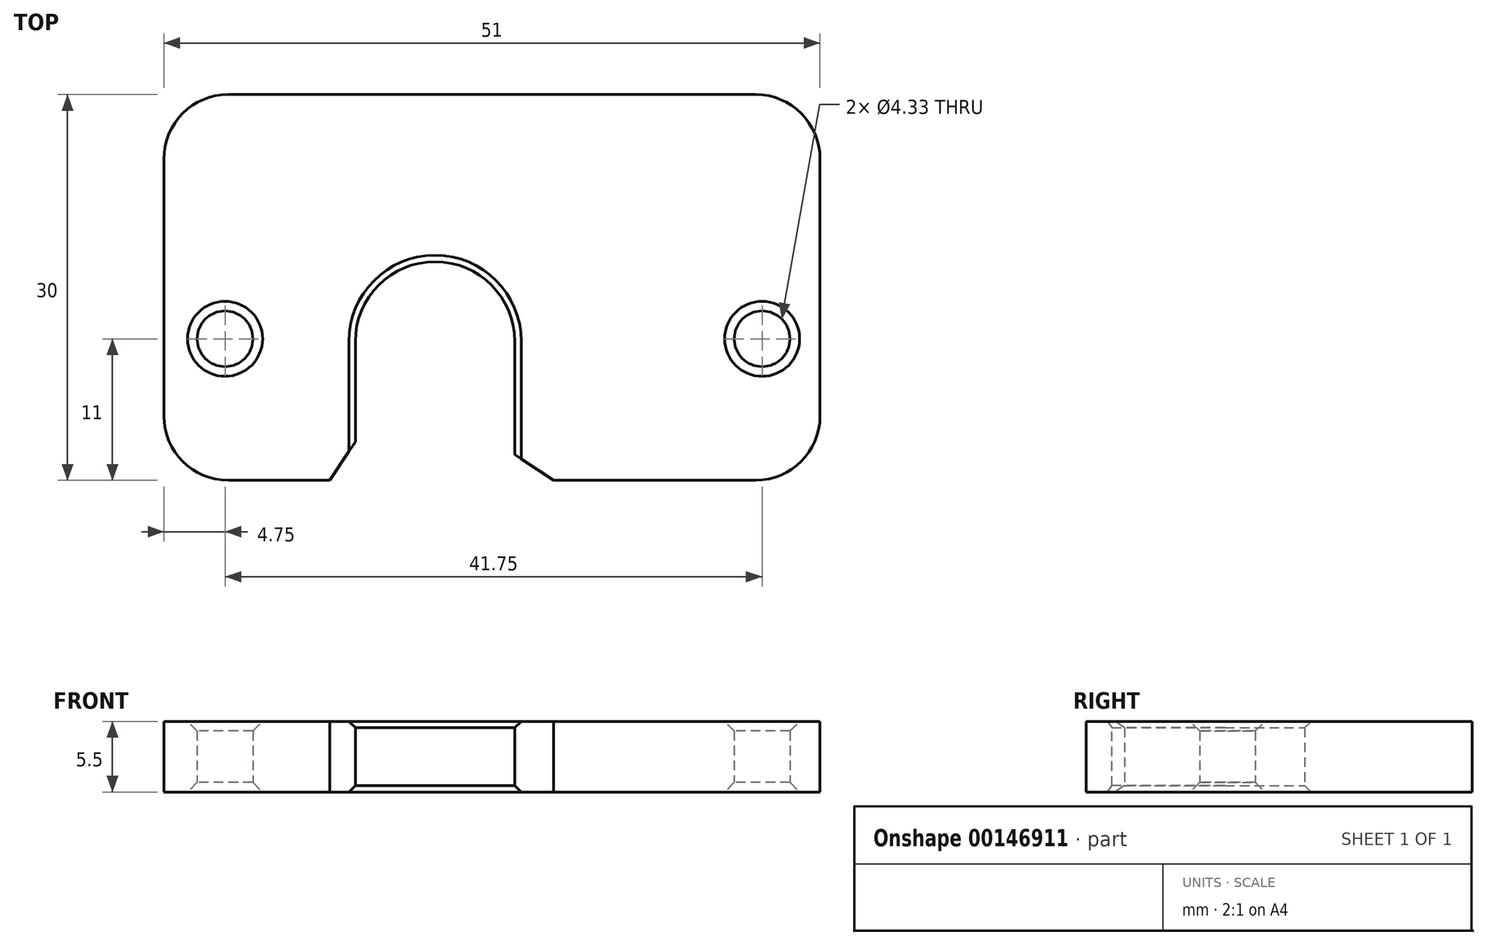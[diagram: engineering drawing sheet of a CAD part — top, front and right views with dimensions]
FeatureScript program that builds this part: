
annotation { "Feature Type Name" : "Feature", "Feature Type Description" : "" }
export const myFeature = defineFeature(function(context is Context, id is Id, definition is map)
    precondition{}
    {
        {
            var Q0;
            Q0=qCreatedBy(makeId("Top.planeOp"),FACE);
            var sketch = newSketch(context, id + "F0", { "sketchPlane" : qUnion([Q0])});
            skLineSegment(sketch, "E0.bottom", {"start": v(-25.5, 11) * mm, "end": v(25.5, 11) * mm});
            skLineSegment(sketch, "E0.top", {"start": v(-25.5, -11) * mm, "end": v(-10.62, -11) * mm});
            skLineSegment(sketch, "E0.left", {"start": v(-25.5, 11) * mm, "end": v(-25.5, -11) * mm});
            skLineSegment(sketch, "E0.right", {"start": v(25.5, 11) * mm, "end": v(25.5, -11) * mm});
            skArc(sketch, "E1", {"start": v(1.77, -0.2) * mm, "mid": v(-4.43, 6) * mm, "end": v(-10.63, -0.2) * mm});
            skLineSegment(sketch, "E2", {"start": v(-10.63, -0.2) * mm, "end": v(-10.62, -11) * mm});
            skLineSegment(sketch, "E3", {"start": v(1.77, -0.2) * mm, "end": v(1.78, -11) * mm});
            skLineSegment(sketch, "E4.trimOffspring", {"start": v(1.78, -11) * mm, "end": v(25.5, -11) * mm});
            skCircle(sketch, "E5", {"center": v(-20.75, 0) * mm, "radius": 2.17 * mm});
            skPoint(sketch, "E6.centerSnap0", {"position": v(-25.5, 0) * mm});
            skCircle(sketch, "E7", {"center": v(21, 0) * mm, "radius": 2.17 * mm});
            skSolve(sketch);
        }
        {
            var Q0;
            Q0=qSketchRegion(id+"F0",true);
            extrude(context, id + "F1", {"entities" : qUnion([Q0]), "depth" : 5.5 * mm});
        }
        {
            var Q0;
            Q0=makeQuery(id+"F1.opExtrude","CAP_EDGE",EDGE,{"disambiguationData":[OSD([sQuery(id+"F0.wireOp",EDGE,"E5")])],"isStart":true});
            var Q1;
            Q1=makeQuery(id+"F1.opExtrude","CAP_EDGE",EDGE,{"disambiguationData":[OSD([sQuery(id+"F0.wireOp",EDGE,"E7")])],"isStart":true});
            var Q2;
            Q2=makeQuery(id+"F1.opExtrude","CAP_EDGE",EDGE,{"disambiguationData":[OSD([sQuery(id+"F0.wireOp",EDGE,"E7")])],"isStart":false});
            var Q3;
            Q3=makeQuery(id+"F1.opExtrude","CAP_EDGE",EDGE,{"disambiguationData":[OSD([sQuery(id+"F0.wireOp",EDGE,"E5")])],"isStart":false});
            chamfer(context, id + "F2", {"entities" : qUnion([Q0, Q1, Q2, Q3]), "width" : .75 * mm, "tangentPropagation" : true});
        }
        {
            var Q0;
            Q0=qCreatedBy(makeId("Top.planeOp"),FACE);
            var sketch = newSketch(context, id + "F3", { "sketchPlane" : qUnion([Q0])});
            skLineSegment(sketch, "E8.0", {"start": v(-25.5, 11) * mm, "end": v(25.5, 11) * mm});
            skLineSegment(sketch, "E9", {"start": v(-25.5, 11) * mm, "end": v(-25.5, 19) * mm});
            skLineSegment(sketch, "E10", {"start": v(-25.5, 19) * mm, "end": v(25.5, 19) * mm});
            skLineSegment(sketch, "E11", {"start": v(25.5, 19) * mm, "end": v(25.5, 11) * mm});
            skSolve(sketch);
        }
        {
            var Q0;
            Q0=qSketchRegion(id+"F3",true);
            var Q1;
            Q1=makeQuery(id+"F1.opExtrude","CAP_FACE",FACE,{"disambiguationData":[OSD([sQuery(id+"F0.wireOp",EDGE,"E0.bottom"),sQuery(id+"F0.wireOp",EDGE,"E0.top"),sQuery(id+"F0.wireOp",EDGE,"E0.left"),sQuery(id+"F0.wireOp",EDGE,"E0.right"),sQuery(id+"F0.wireOp",EDGE,"E1"),sQuery(id+"F0.wireOp",EDGE,"E2"),sQuery(id+"F0.wireOp",EDGE,"E3"),sQuery(id+"F0.wireOp",EDGE,"E4.trimOffspring"),sQuery(id+"F0.wireOp",EDGE,"E5"),sQuery(id+"F0.wireOp",EDGE,"E7")])],"isStart":false});
            extrude(context, id + "F4", {"entities" : qUnion([Q0]), "operationType" : NewBodyOperationType.ADD, "endBound" : BoundingType.UP_TO_SURFACE, "endBoundEntityFace" : qUnion([Q1]), "depth" : 6 * mm});
        }
        {
            var Q0;
            Q0=makeQuery(id+"F1.opExtrude","CAP_EDGE",EDGE,{"disambiguationData":[OSD([sQuery(id+"F0.wireOp",EDGE,"E1")])],"isStart":false});
            var Q1;
            Q1=makeQuery(id+"F1.opExtrude","CAP_EDGE",EDGE,{"disambiguationData":[OSD([sQuery(id+"F0.wireOp",EDGE,"E1")])],"isStart":true});
            var Q2;
            Q2=makeQuery(id+"F1.opExtrude","CAP_EDGE",EDGE,{"disambiguationData":[OSD([sQuery(id+"F0.wireOp",EDGE,"E2")])],"isStart":false});
            var Q3;
            {var subQ0=sQuery(id+"F0.wireOp",EDGE,"E7");var subQ1=sQuery(id+"F0.wireOp",EDGE,"E5");var subQ2=sQuery(id+"F0.wireOp",EDGE,"E4.trimOffspring");var subQ3=sQuery(id+"F0.wireOp",EDGE,"E3");var subQ4=sQuery(id+"F0.wireOp",EDGE,"E2");var subQ5=sQuery(id+"F0.wireOp",EDGE,"E1");var subQ6=sQuery(id+"F0.wireOp",EDGE,"E0.right");var subQ7=sQuery(id+"F0.wireOp",EDGE,"E0.left");var subQ8=sQuery(id+"F0.wireOp",EDGE,"E0.top");var subQ9=sQuery(id+"F0.wireOp",EDGE,"E0.bottom");Q3=makeQuery(id+"F8.opChamfer","BLEND_EDGE",EDGE,{"blendedFrom":[makeQuery(id+"F1.opExtrude","SWEPT_EDGE",EDGE,{"disambiguationData":[OSD([subQ8,subQ4])]}),makeQuery(id+"F4.boolean.opBoolean","MERGE",FACE,{"derivedFrom":[makeQuery(id+"F1.opExtrude","CAP_FACE",FACE,{"disambiguationData":[OSD([subQ9,subQ8,subQ7,subQ6,subQ5,subQ4,subQ3,subQ2,subQ1,subQ0])],"isStart":false}),makeQuery(id+"F4.opExtrude","CAP_FACE",FACE,{"disambiguationData":[OSD([subQ9,subQ8,subQ7,subQ6,subQ5,subQ4,subQ3,subQ2,subQ1,subQ0])],"isStart":false})]})],"blendedInto":[makeQuery(id+"F4.boolean.opBoolean","MERGE",FACE,{"derivedFrom":[makeQuery(id+"F1.opExtrude","CAP_FACE",FACE,{"disambiguationData":[OSD([subQ9,subQ8,subQ7,subQ6,subQ5,subQ4,subQ3,subQ2,subQ1,subQ0])],"isStart":false}),makeQuery(id+"F4.opExtrude","CAP_FACE",FACE,{"disambiguationData":[OSD([subQ9,subQ8,subQ7,subQ6,subQ5,subQ4,subQ3,subQ2,subQ1,subQ0])],"isStart":false})]})]});}
            var Q4;
            {var subQ0=sQuery(id+"F0.wireOp",EDGE,"E2");var subQ1=sQuery(id+"F0.wireOp",EDGE,"E0.top");Q4=makeQuery(id+"F8.opChamfer","BLEND_EDGE",EDGE,{"blendedFrom":[makeQuery(id+"F1.opExtrude","SWEPT_EDGE",EDGE,{"disambiguationData":[OSD([subQ1,subQ0])]}),makeQuery(id+"FEx9i5uBCyc1I2h_1.boolean.opBoolean","MERGE",FACE,{"derivedFrom":[makeQuery(id+"F4.boolean.opBoolean","MERGE",FACE,{"derivedFrom":[makeQuery(id+"F1.opExtrude","CAP_FACE",FACE,{"disambiguationData":[OSD([sQuery(id+"F0.wireOp",EDGE,"E0.bottom"),subQ1,sQuery(id+"F0.wireOp",EDGE,"E0.left"),sQuery(id+"F0.wireOp",EDGE,"E0.right"),sQuery(id+"F0.wireOp",EDGE,"E1"),subQ0,sQuery(id+"F0.wireOp",EDGE,"E3"),sQuery(id+"F0.wireOp",EDGE,"E4.trimOffspring"),sQuery(id+"F0.wireOp",EDGE,"E5"),sQuery(id+"F0.wireOp",EDGE,"E7")])],"isStart":true}),makeQuery(id+"F4.opExtrude","CAP_FACE",FACE,{"disambiguationData":[OSD([sQuery(id+"F3.wireOp",EDGE,"E8.0"),sQuery(id+"F3.wireOp",EDGE,"E9"),sQuery(id+"F3.wireOp",EDGE,"E10"),sQuery(id+"F3.wireOp",EDGE,"E11")])],"isStart":true})]}),makeQuery(id+"FEx9i5uBCyc1I2h_1.opExtrude","CAP_FACE",FACE,{"disambiguationData":[OSD([sQuery(id+"F6.wireOp",EDGE,"E15"),sQuery(id+"F6.wireOp",EDGE,"E16"),sQuery(id+"F6.wireOp",EDGE,"E17"),sQuery(id+"F6.wireOp",EDGE,"E18")])],"isStart":true}),makeQuery(id+"FEx9i5uBCyc1I2h_1.opExtrude","CAP_FACE",FACE,{"disambiguationData":[OSD([sQuery(id+"F6.wireOp",EDGE,"E19.MirrorCS"),sQuery(id+"F6.wireOp",EDGE,"E20.MirrorCS"),sQuery(id+"F6.wireOp",EDGE,"E21.MirrorCS"),sQuery(id+"F6.wireOp",EDGE,"E23.MirrorCS")])],"isStart":true})]})],"blendedInto":[makeQuery(id+"FEx9i5uBCyc1I2h_1.boolean.opBoolean","MERGE",FACE,{"derivedFrom":[makeQuery(id+"F4.boolean.opBoolean","MERGE",FACE,{"derivedFrom":[makeQuery(id+"F1.opExtrude","CAP_FACE",FACE,{"disambiguationData":[OSD([sQuery(id+"F0.wireOp",EDGE,"E0.bottom"),subQ1,sQuery(id+"F0.wireOp",EDGE,"E0.left"),sQuery(id+"F0.wireOp",EDGE,"E0.right"),sQuery(id+"F0.wireOp",EDGE,"E1"),subQ0,sQuery(id+"F0.wireOp",EDGE,"E3"),sQuery(id+"F0.wireOp",EDGE,"E4.trimOffspring"),sQuery(id+"F0.wireOp",EDGE,"E5"),sQuery(id+"F0.wireOp",EDGE,"E7")])],"isStart":true}),makeQuery(id+"F4.opExtrude","CAP_FACE",FACE,{"disambiguationData":[OSD([sQuery(id+"F3.wireOp",EDGE,"E8.0"),sQuery(id+"F3.wireOp",EDGE,"E9"),sQuery(id+"F3.wireOp",EDGE,"E10"),sQuery(id+"F3.wireOp",EDGE,"E11")])],"isStart":true})]}),makeQuery(id+"FEx9i5uBCyc1I2h_1.opExtrude","CAP_FACE",FACE,{"disambiguationData":[OSD([sQuery(id+"F6.wireOp",EDGE,"E15"),sQuery(id+"F6.wireOp",EDGE,"E16"),sQuery(id+"F6.wireOp",EDGE,"E17"),sQuery(id+"F6.wireOp",EDGE,"E18")])],"isStart":true}),makeQuery(id+"FEx9i5uBCyc1I2h_1.opExtrude","CAP_FACE",FACE,{"disambiguationData":[OSD([sQuery(id+"F6.wireOp",EDGE,"E19.MirrorCS"),sQuery(id+"F6.wireOp",EDGE,"E20.MirrorCS"),sQuery(id+"F6.wireOp",EDGE,"E21.MirrorCS"),sQuery(id+"F6.wireOp",EDGE,"E23.MirrorCS")])],"isStart":true})]})]});}
            var Q5;
            Q5=makeQuery(id+"F1.opExtrude","CAP_EDGE",EDGE,{"disambiguationData":[OSD([sQuery(id+"F0.wireOp",EDGE,"E2")])],"isStart":true});
            var Q6;
            Q6=makeQuery(id+"F1.opExtrude","CAP_EDGE",EDGE,{"disambiguationData":[OSD([sQuery(id+"F0.wireOp",EDGE,"E3")])],"isStart":true});
            var Q7;
            {var subQ0=sQuery(id+"F0.wireOp",EDGE,"E4.trimOffspring");var subQ1=sQuery(id+"F0.wireOp",EDGE,"E3");Q7=makeQuery(id+"F8.opChamfer","BLEND_EDGE",EDGE,{"blendedFrom":[makeQuery(id+"F1.opExtrude","SWEPT_EDGE",EDGE,{"disambiguationData":[OSD([subQ1,subQ0])]}),makeQuery(id+"FEx9i5uBCyc1I2h_1.boolean.opBoolean","MERGE",FACE,{"derivedFrom":[makeQuery(id+"F4.boolean.opBoolean","MERGE",FACE,{"derivedFrom":[makeQuery(id+"F1.opExtrude","CAP_FACE",FACE,{"disambiguationData":[OSD([sQuery(id+"F0.wireOp",EDGE,"E0.bottom"),sQuery(id+"F0.wireOp",EDGE,"E0.top"),sQuery(id+"F0.wireOp",EDGE,"E0.left"),sQuery(id+"F0.wireOp",EDGE,"E0.right"),sQuery(id+"F0.wireOp",EDGE,"E1"),sQuery(id+"F0.wireOp",EDGE,"E2"),subQ1,subQ0,sQuery(id+"F0.wireOp",EDGE,"E5"),sQuery(id+"F0.wireOp",EDGE,"E7")])],"isStart":true}),makeQuery(id+"F4.opExtrude","CAP_FACE",FACE,{"disambiguationData":[OSD([sQuery(id+"F3.wireOp",EDGE,"E8.0"),sQuery(id+"F3.wireOp",EDGE,"E9"),sQuery(id+"F3.wireOp",EDGE,"E10"),sQuery(id+"F3.wireOp",EDGE,"E11")])],"isStart":true})]}),makeQuery(id+"FEx9i5uBCyc1I2h_1.opExtrude","CAP_FACE",FACE,{"disambiguationData":[OSD([sQuery(id+"F6.wireOp",EDGE,"E15"),sQuery(id+"F6.wireOp",EDGE,"E16"),sQuery(id+"F6.wireOp",EDGE,"E17"),sQuery(id+"F6.wireOp",EDGE,"E18")])],"isStart":true}),makeQuery(id+"FEx9i5uBCyc1I2h_1.opExtrude","CAP_FACE",FACE,{"disambiguationData":[OSD([sQuery(id+"F6.wireOp",EDGE,"E19.MirrorCS"),sQuery(id+"F6.wireOp",EDGE,"E20.MirrorCS"),sQuery(id+"F6.wireOp",EDGE,"E21.MirrorCS"),sQuery(id+"F6.wireOp",EDGE,"E23.MirrorCS")])],"isStart":true})]})],"blendedInto":[makeQuery(id+"FEx9i5uBCyc1I2h_1.boolean.opBoolean","MERGE",FACE,{"derivedFrom":[makeQuery(id+"F4.boolean.opBoolean","MERGE",FACE,{"derivedFrom":[makeQuery(id+"F1.opExtrude","CAP_FACE",FACE,{"disambiguationData":[OSD([sQuery(id+"F0.wireOp",EDGE,"E0.bottom"),sQuery(id+"F0.wireOp",EDGE,"E0.top"),sQuery(id+"F0.wireOp",EDGE,"E0.left"),sQuery(id+"F0.wireOp",EDGE,"E0.right"),sQuery(id+"F0.wireOp",EDGE,"E1"),sQuery(id+"F0.wireOp",EDGE,"E2"),subQ1,subQ0,sQuery(id+"F0.wireOp",EDGE,"E5"),sQuery(id+"F0.wireOp",EDGE,"E7")])],"isStart":true}),makeQuery(id+"F4.opExtrude","CAP_FACE",FACE,{"disambiguationData":[OSD([sQuery(id+"F3.wireOp",EDGE,"E8.0"),sQuery(id+"F3.wireOp",EDGE,"E9"),sQuery(id+"F3.wireOp",EDGE,"E10"),sQuery(id+"F3.wireOp",EDGE,"E11")])],"isStart":true})]}),makeQuery(id+"FEx9i5uBCyc1I2h_1.opExtrude","CAP_FACE",FACE,{"disambiguationData":[OSD([sQuery(id+"F6.wireOp",EDGE,"E15"),sQuery(id+"F6.wireOp",EDGE,"E16"),sQuery(id+"F6.wireOp",EDGE,"E17"),sQuery(id+"F6.wireOp",EDGE,"E18")])],"isStart":true}),makeQuery(id+"FEx9i5uBCyc1I2h_1.opExtrude","CAP_FACE",FACE,{"disambiguationData":[OSD([sQuery(id+"F6.wireOp",EDGE,"E19.MirrorCS"),sQuery(id+"F6.wireOp",EDGE,"E20.MirrorCS"),sQuery(id+"F6.wireOp",EDGE,"E21.MirrorCS"),sQuery(id+"F6.wireOp",EDGE,"E23.MirrorCS")])],"isStart":true})]})]});}
            var Q8;
            Q8=makeQuery(id+"F1.opExtrude","CAP_EDGE",EDGE,{"disambiguationData":[OSD([sQuery(id+"F0.wireOp",EDGE,"E3")])],"isStart":false});
            var Q9;
            {var subQ0=sQuery(id+"F0.wireOp",EDGE,"E7");var subQ1=sQuery(id+"F0.wireOp",EDGE,"E5");var subQ2=sQuery(id+"F0.wireOp",EDGE,"E4.trimOffspring");var subQ3=sQuery(id+"F0.wireOp",EDGE,"E3");var subQ4=sQuery(id+"F0.wireOp",EDGE,"E2");var subQ5=sQuery(id+"F0.wireOp",EDGE,"E1");var subQ6=sQuery(id+"F0.wireOp",EDGE,"E0.right");var subQ7=sQuery(id+"F0.wireOp",EDGE,"E0.left");var subQ8=sQuery(id+"F0.wireOp",EDGE,"E0.top");var subQ9=sQuery(id+"F0.wireOp",EDGE,"E0.bottom");Q9=makeQuery(id+"F8.opChamfer","BLEND_EDGE",EDGE,{"blendedFrom":[makeQuery(id+"F1.opExtrude","SWEPT_EDGE",EDGE,{"disambiguationData":[OSD([subQ3,subQ2])]}),makeQuery(id+"F4.boolean.opBoolean","MERGE",FACE,{"derivedFrom":[makeQuery(id+"F1.opExtrude","CAP_FACE",FACE,{"disambiguationData":[OSD([subQ9,subQ8,subQ7,subQ6,subQ5,subQ4,subQ3,subQ2,subQ1,subQ0])],"isStart":false}),makeQuery(id+"F4.opExtrude","CAP_FACE",FACE,{"disambiguationData":[OSD([subQ9,subQ8,subQ7,subQ6,subQ5,subQ4,subQ3,subQ2,subQ1,subQ0])],"isStart":false})]})],"blendedInto":[makeQuery(id+"F4.boolean.opBoolean","MERGE",FACE,{"derivedFrom":[makeQuery(id+"F1.opExtrude","CAP_FACE",FACE,{"disambiguationData":[OSD([subQ9,subQ8,subQ7,subQ6,subQ5,subQ4,subQ3,subQ2,subQ1,subQ0])],"isStart":false}),makeQuery(id+"F4.opExtrude","CAP_FACE",FACE,{"disambiguationData":[OSD([subQ9,subQ8,subQ7,subQ6,subQ5,subQ4,subQ3,subQ2,subQ1,subQ0])],"isStart":false})]})]});}
            chamfer(context, id + "F5", {"entities" : qUnion([Q0, Q1, Q2, Q3, Q4, Q5, Q6, Q7, Q8, Q9]), "width" : .5 * mm, "tangentPropagation" : true});
        }
        {
            var Q0;
            Q0=qCreatedBy(makeId("Top.planeOp"),FACE);
            var sketch = newSketch(context, id + "F6", { "sketchPlane" : qUnion([Q0])});
            skArc(sketch, "E12.0", {"start": v(1.77, -0.2) * mm, "mid": v(-4.43, 6) * mm, "end": v(-10.63, -0.2) * mm, "construction": true});
            skLineSegment(sketch, "E13.0", {"start": v(-25.5, 19) * mm, "end": v(25.5, 19) * mm, "construction": true});
            skLineSegment(sketch, "E14", {"start": v(-4.43, 32.8) * mm, "end": v(-4.43, -0.2) * mm, "construction": true});
            skLineSegment(sketch, "E15", {"start": v(-8.73, 36) * mm, "end": v(-6.23, 36) * mm});
            skLineSegment(sketch, "E16", {"start": v(-6.23, 36) * mm, "end": v(-6.23, 19) * mm});
            skLineSegment(sketch, "E17", {"start": v(-6.23, 19) * mm, "end": v(-8.73, 19) * mm});
            skLineSegment(sketch, "E18", {"start": v(-8.73, 19) * mm, "end": v(-8.73, 36) * mm});
            skLineSegment(sketch, "E19.MirrorCS", {"start": v(-2.63, 36) * mm, "end": v(-2.63, 19) * mm});
            skLineSegment(sketch, "E20.MirrorCS", {"start": v(-0.13, 19) * mm, "end": v(-0.13, 36) * mm});
            skLineSegment(sketch, "E21.MirrorCS", {"start": v(-0.13, 36) * mm, "end": v(-2.63, 36) * mm});
            skLineSegment(sketch, "E22.MirrorCS", {"start": v(-4.42, 5.2) * mm, "end": v(-4.43, 38.2) * mm, "construction": true});
            skLineSegment(sketch, "E23.MirrorCS", {"start": v(-2.63, 19) * mm, "end": v(-0.13, 19) * mm});
            skSolve(sketch);
        }
        {
            var Q0;
            Q0=makeQuery(id+"F1.opExtrude","SWEPT_EDGE",EDGE,{"disambiguationData":[OSD([sQuery(id+"F0.wireOp",EDGE,"E0.right"),sQuery(id+"F0.wireOp",EDGE,"E4.trimOffspring")])]});
            var Q1;
            Q1=makeQuery(id+"F1.opExtrude","SWEPT_EDGE",EDGE,{"disambiguationData":[OSD([sQuery(id+"F0.wireOp",EDGE,"E0.top"),sQuery(id+"F0.wireOp",EDGE,"E0.left")])]});
            var Q2;
            Q2=makeQuery(id+"F4.opExtrude","SWEPT_EDGE",EDGE,{"disambiguationData":[OSD([sQuery(id+"F3.wireOp",EDGE,"E10"),sQuery(id+"F3.wireOp",EDGE,"E11")])]});
            var Q3;
            Q3=makeQuery(id+"F4.opExtrude","SWEPT_EDGE",EDGE,{"disambiguationData":[OSD([sQuery(id+"F3.wireOp",EDGE,"E9"),sQuery(id+"F3.wireOp",EDGE,"E10")])]});
            fillet(context, id + "F7", {"entities" : qUnion([Q0, Q1, Q2, Q3]), "radius" : 5 * mm, "tangentPropagation" : true, "allowEdgeOverflow" : false});
        }
        {
            var Q0;
            Q0=makeQuery(id+"F1.opExtrude","SWEPT_EDGE",EDGE,{"disambiguationData":[OSD([sQuery(id+"F0.wireOp",EDGE,"E0.top"),sQuery(id+"F0.wireOp",EDGE,"E2")])]});
            var Q1;
            Q1=makeQuery(id+"F1.opExtrude","SWEPT_EDGE",EDGE,{"disambiguationData":[OSD([sQuery(id+"F0.wireOp",EDGE,"E3"),sQuery(id+"F0.wireOp",EDGE,"E4.trimOffspring")])]});
            chamfer(context, id + "F8", {"entities" : qUnion([Q0, Q1]), "chamferType" : ChamferType.TWO_OFFSETS, "width1" : 3 * mm, "oppositeDirection" : false, "width2" : 2 * mm, "tangentPropagation" : true});
        }
    });
